# Revit family: Urinals-Commercial_UT104E_TOTO
name_source: partatom
category: Plumbing Fixtures
revit_build: Autodesk Revit Architecture 2013 (Build: 20130531_2115(x64)
units: mm (PartAtom-declared; Revit-internal decimal feet)

## types (1)
- UT104E
    04 CSI = 22 42 13
    95 CSI = 15410
    ADA Compliant = Yes
    Assembly Code = D2010210
    Available in SanoGloss = No
    CAD Drawing URL = http://assets.totousa.com
    CW Connection = Yes
    CWFU = 0
    Certifications = IAPMO(cUPC), State of Massachusetts, City of Los Angeles
    Code Compliance = UPC, IPC, NSPC, NPC Canada, and others
    Cold Water Connection Diameter = 0' - 0 1/2"
    Cold Water Connection NPT Radius = 3/8"
    Cold Water Connection Radius = 0' - 0 1/2"
    Cold Water Connector = Cold Water Connection
    Color Availability = #01 Cotton, #03 Bone, #12 Sedona Beige
    Default Elevation = 1' - 11 1/2"
    Depth = 1' - 2"
    Description = Commercial Washout High Efficiency Urinal, 0.5 GPF - ADA
    Finish = Vitreous China - TOTO - 01 Cotton
    Flush Valve Model = Flush Valve Model : TEU1LN12
    Gallons Per Flush = 0.5 gal
    HW Connection = No
    HWFU = 0
    Height = 1' - 10"
    Industry Standards = Meets and exceeds ASME A112.19.2/CSA B45.1
    Manufacturer = TOTO USA, Inc.
    Manufacturer Fax = (770) 282-0002
    Material = Vitreous China
    Model = UT104E
    Mount Type = Wall
    Sanitary Connector = Sanitary Connection
    Shipping Weight = 34.50 lb
    Spec Sheet URL = http://assets.totousa.com
    Style = Commercial
    Subcategory = Urinals
    Toto BIM Number = BM-00026
    URL = http://www.totousa.com
    Vent Connection = Yes
    WFU = 0
    Warranty = One Year Limited Warranty
    Warranty URL = http://www.totousa.com
    Waste Connection = Yes
    Waste Connection NPT Radius = 0' - 1"
    Width = 1' - 1"

## geometry (parser evidence)
native form markers: Blend x2, Sweep x5
no freeform markers — native parametric forms only
